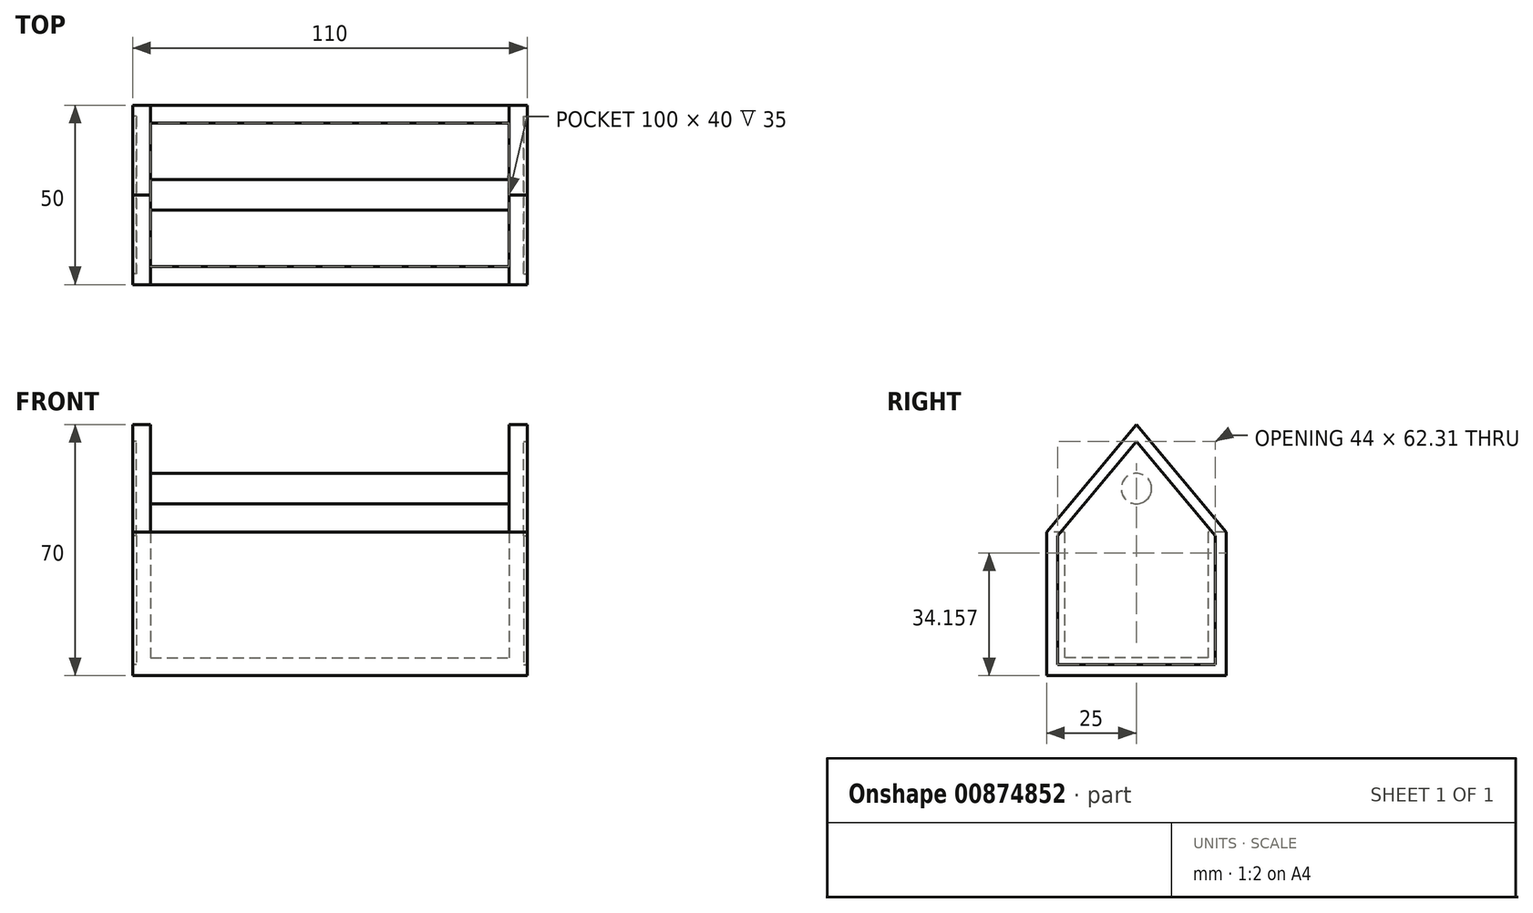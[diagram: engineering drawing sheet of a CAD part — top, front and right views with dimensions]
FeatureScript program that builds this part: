
annotation { "Feature Type Name" : "Feature", "Feature Type Description" : "" }
export const myFeature = defineFeature(function(context is Context, id is Id, definition is map)
    precondition{}
    {
        {
            var Q0;
            Q0=qCreatedBy(makeId("Top.planeOp"),FACE);
            var sketch = newSketch(context, id + "F0", { "sketchPlane" : qUnion([Q0])});
            skLineSegment(sketch, "E0.bottom", {"start": v(-50.43, 19.12) * mm, "end": v(59.57, 19.12) * mm});
            skLineSegment(sketch, "E0.top", {"start": v(-50.43, -30.88) * mm, "end": v(59.57, -30.88) * mm});
            skLineSegment(sketch, "E0.left", {"start": v(-50.43, 19.12) * mm, "end": v(-50.43, -30.88) * mm});
            skLineSegment(sketch, "E0.right", {"start": v(59.57, 19.12) * mm, "end": v(59.57, -30.88) * mm});
            skSolve(sketch);
        }
        {
            var Q0;
            Q0 = qSketchRegion(id + "F0", true);
            extrude(context, id + "F1", {"entities" : qUnion([Q0]), "depth" : 5 * mm, "offsetDistance" : 25 * mm});
        }
        {
            var Q0;
            Q0=makeQuery(id+"F1.opExtrude","CAP_FACE",FACE,{"disambiguationData":[OSD([sQuery(id+"F0.wireOp",EDGE,"E0.bottom"),sQuery(id+"F0.wireOp",EDGE,"E0.top"),sQuery(id+"F0.wireOp",EDGE,"E0.left"),sQuery(id+"F0.wireOp",EDGE,"E0.right")])],"isStart":false});
            var sketch = newSketch(context, id + "F2", { "sketchPlane" : qUnion([Q0])});
            skLineSegment(sketch, "E1.bottom", {"start": v(-50.43, 19.12) * mm, "end": v(59.57, 19.12) * mm});
            skLineSegment(sketch, "E1.top", {"start": v(-50.43, 14.12) * mm, "end": v(59.57, 14.12) * mm});
            skLineSegment(sketch, "E1.left", {"start": v(-50.43, 19.12) * mm, "end": v(-50.43, 14.12) * mm});
            skLineSegment(sketch, "E1.right", {"start": v(59.57, 19.12) * mm, "end": v(59.57, 14.12) * mm});
            skLineSegment(sketch, "E2.bottom", {"start": v(59.57, -30.88) * mm, "end": v(-50.43, -30.88) * mm});
            skLineSegment(sketch, "E2.top", {"start": v(59.57, -25.88) * mm, "end": v(-50.43, -25.88) * mm});
            skLineSegment(sketch, "E2.left", {"start": v(59.57, -30.88) * mm, "end": v(59.57, -25.88) * mm});
            skLineSegment(sketch, "E2.right", {"start": v(-50.43, -30.88) * mm, "end": v(-50.43, -25.88) * mm});
            skLineSegment(sketch, "E3.bottom", {"start": v(-50.43, 14.12) * mm, "end": v(-45.43, 14.12) * mm});
            skLineSegment(sketch, "E3.top", {"start": v(-50.43, -25.88) * mm, "end": v(-45.43, -25.88) * mm});
            skLineSegment(sketch, "E3.left", {"start": v(-50.43, 14.12) * mm, "end": v(-50.43, -25.88) * mm});
            skLineSegment(sketch, "E3.right", {"start": v(-45.43, 14.12) * mm, "end": v(-45.43, -25.88) * mm});
            skLineSegment(sketch, "E4.bottom", {"start": v(59.57, 14.12) * mm, "end": v(54.57, 14.12) * mm});
            skLineSegment(sketch, "E4.top", {"start": v(59.57, -25.88) * mm, "end": v(54.57, -25.88) * mm});
            skLineSegment(sketch, "E4.left", {"start": v(59.57, 14.12) * mm, "end": v(59.57, -25.88) * mm});
            skLineSegment(sketch, "E4.right", {"start": v(54.57, 14.12) * mm, "end": v(54.57, -25.88) * mm});
            skSolve(sketch);
        }
        {
            var Q0;
            Q0 = qSketchRegion(id + "F2", true);
            extrude(context, id + "F3", {"entities" : qUnion([Q0]), "operationType" : NewBodyOperationType.ADD, "depth" : 35 * mm, "offsetDistance" : 25 * mm});
        }
        {
            var Q0;
            Q0=makeQuery(id+"F3.boolean.opBoolean","MERGE",FACE,{"derivedFrom":[makeQuery(id+"F1.opExtrude","SWEPT_FACE",FACE,{"disambiguationData":[OSD([sQuery(id+"F0.wireOp",EDGE,"E0.left")])]}),makeQuery(id+"F3.opExtrude","SWEPT_FACE",FACE,{"disambiguationData":[OSD([sQuery(id+"F2.wireOp",EDGE,"E1.left"),sQuery(id+"F2.wireOp",EDGE,"E2.right"),sQuery(id+"F2.wireOp",EDGE,"E3.left")])]})]});
            var sketch = newSketch(context, id + "F4", { "sketchPlane" : qUnion([Q0])});
            skLineSegment(sketch, "E5", {"start": v(-19.12, 40) * mm, "end": v(5.88, 70) * mm});
            skLineSegment(sketch, "E6", {"start": v(5.88, 70) * mm, "end": v(5.88, 40) * mm});
            skLineSegment(sketch, "E7", {"start": v(30.88, 40) * mm, "end": v(5.88, 70) * mm});
            skSolve(sketch);
        }
        {
            var Q0;
            Q0 = qSketchRegion(id + "F4", true);
            var Q1;
            {var subQ0=sQuery(id+"F4.wireOp",EDGE,"E6");Q1=makeQuery(id+"F4.imprint","IMPRINT",FACE,{"disambiguationData":[TD([[makeQuery(id+"F4.imprint","IMPRINT",EDGE,{"derivedFrom":subQ0}),1.0]])]});}
            var Q2;
            {var subQ0=sQuery(id+"F4.wireOp",EDGE,"E5");Q2=makeQuery(id+"F4.imprint","IMPRINT",FACE,{"disambiguationData":[TD([[makeQuery(id+"F4.imprint","IMPRINT",EDGE,{"derivedFrom":subQ0}),-1.0]])]});}
            extrude(context, id + "F5", {"entities" : qUnion([Q0, Q1, Q2]), "operationType" : NewBodyOperationType.ADD, "oppositeDirection" : true, "depth" : 5 * mm, "offsetDistance" : 25 * mm});
        }
        {
            var Q0;
            Q0=makeQuery(id+"F3.boolean.opBoolean","MERGE",FACE,{"derivedFrom":[makeQuery(id+"F1.opExtrude","SWEPT_FACE",FACE,{"disambiguationData":[OSD([sQuery(id+"F0.wireOp",EDGE,"E0.right")])]}),makeQuery(id+"F3.opExtrude","SWEPT_FACE",FACE,{"disambiguationData":[OSD([sQuery(id+"F2.wireOp",EDGE,"E1.right"),sQuery(id+"F2.wireOp",EDGE,"E2.left"),sQuery(id+"F2.wireOp",EDGE,"E4.left")])]})]});
            var sketch = newSketch(context, id + "F6", { "sketchPlane" : qUnion([Q0])});
            skLineSegment(sketch, "E8", {"start": v(-5.88, 40) * mm, "end": v(-5.88, 70) * mm});
            skLineSegment(sketch, "E9", {"start": v(-5.88, 70) * mm, "end": v(-30.88, 40) * mm});
            skLineSegment(sketch, "E10", {"start": v(19.12, 40) * mm, "end": v(-5.88, 70) * mm});
            skSolve(sketch);
        }
        {
            var Q0;
            Q0 = qSketchRegion(id + "F6", true);
            var Q1;
            {var subQ0=sQuery(id+"F6.wireOp",EDGE,"E8");Q1=makeQuery(id+"F6.imprint","IMPRINT",FACE,{"disambiguationData":[TD([[makeQuery(id+"F6.imprint","IMPRINT",EDGE,{"derivedFrom":subQ0}),1.0]])]});}
            var Q2;
            {var subQ0=sQuery(id+"F6.wireOp",EDGE,"E8");Q2=makeQuery(id+"F6.imprint","IMPRINT",FACE,{"disambiguationData":[TD([[makeQuery(id+"F6.imprint","IMPRINT",EDGE,{"derivedFrom":subQ0}),-1.0]])]});}
            extrude(context, id + "F7", {"entities" : qUnion([Q0, Q1, Q2]), "operationType" : NewBodyOperationType.ADD, "oppositeDirection" : true, "depth" : 5 * mm, "offsetDistance" : 25 * mm});
        }
        {
            var Q0;
            Q0=makeQuery(id+"F5.boolean.opBoolean","MERGE",FACE,{"derivedFrom":[makeQuery(id+"F3.opExtrude","SWEPT_FACE",FACE,{"disambiguationData":[OSD([sQuery(id+"F2.wireOp",EDGE,"E3.right")])]}),makeQuery(id+"F5.opExtrude","CAP_FACE",FACE,{"disambiguationData":[OSD([sQuery(id+"F2.wireOp",EDGE,"E1.left"),sQuery(id+"F2.wireOp",EDGE,"E2.right"),sQuery(id+"F2.wireOp",EDGE,"E3.left"),sQuery(id+"F4.wireOp",EDGE,"E5"),sQuery(id+"F4.wireOp",EDGE,"E7")])],"isStart":false})]});
            var sketch = newSketch(context, id + "F8", { "sketchPlane" : qUnion([Q0])});
            skLineSegment(sketch, "E11", {"start": v(-5.88, 70) * mm, "end": v(-5.88, 34.24) * mm});
            skCircle(sketch, "E12", {"center": v(-5.88, 52.12) * mm, "radius": 4.25 * mm});
            skSolve(sketch);
        }
        {
            var Q0;
            Q0 = qSketchRegion(id + "F8", true);
            extrude(context, id + "F9", {"entities" : qUnion([Q0]), "operationType" : NewBodyOperationType.ADD, "depth" : 101 * mm, "offsetDistance" : 25 * mm});
        }
        {
            var Q0;
            {var subQ0=sQuery(id+"F2.wireOp",EDGE,"E4.left");var subQ1=sQuery(id+"F2.wireOp",EDGE,"E2.left");var subQ2=sQuery(id+"F2.wireOp",EDGE,"E1.right");Q0=makeQuery(id+"F7.boolean.opBoolean","MERGE",FACE,{"derivedFrom":[makeQuery(id+"F3.boolean.opBoolean","MERGE",FACE,{"derivedFrom":[makeQuery(id+"F1.opExtrude","SWEPT_FACE",FACE,{"disambiguationData":[OSD([sQuery(id+"F0.wireOp",EDGE,"E0.right")])]}),makeQuery(id+"F3.opExtrude","SWEPT_FACE",FACE,{"disambiguationData":[OSD([subQ2,subQ1,subQ0])]})]}),makeQuery(id+"F7.opExtrude","CAP_FACE",FACE,{"disambiguationData":[OSD([subQ2,subQ1,subQ0,sQuery(id+"F6.wireOp",EDGE,"E9"),sQuery(id+"F6.wireOp",EDGE,"E10")])],"isStart":true})]});}
            var sketch = newSketch(context, id + "F10", { "sketchPlane" : qUnion([Q0])});
            skLineSegment(sketch, "E13", {"start": v(-27.88, 3) * mm, "end": v(16.12, 3) * mm});
            skLineSegment(sketch, "E14", {"start": v(16.12, 3) * mm, "end": v(16.12, 38.91) * mm});
            skLineSegment(sketch, "E15", {"start": v(16.12, 38.91) * mm, "end": v(-5.88, 65.31) * mm});
            skLineSegment(sketch, "E16", {"start": v(-5.88, 65.31) * mm, "end": v(-27.88, 38.91) * mm});
            skLineSegment(sketch, "E17", {"start": v(-27.88, 38.91) * mm, "end": v(-27.88, 3) * mm});
            skSolve(sketch);
        }
        {
            var Q0;
            Q0 = qSketchRegion(id + "F10", true);
            extrude(context, id + "F11", {"entities" : qUnion([Q0]), "operationType" : NewBodyOperationType.REMOVE, "oppositeDirection" : true, "depth" : 1 * mm, "offsetDistance" : 25 * mm});
        }
        {
            var Q0;
            {var subQ0=sQuery(id+"F2.wireOp",EDGE,"E3.left");var subQ1=sQuery(id+"F2.wireOp",EDGE,"E2.right");var subQ2=sQuery(id+"F2.wireOp",EDGE,"E1.left");Q0=makeQuery(id+"F5.boolean.opBoolean","MERGE",FACE,{"derivedFrom":[makeQuery(id+"F3.boolean.opBoolean","MERGE",FACE,{"derivedFrom":[makeQuery(id+"F1.opExtrude","SWEPT_FACE",FACE,{"disambiguationData":[OSD([sQuery(id+"F0.wireOp",EDGE,"E0.left")])]}),makeQuery(id+"F3.opExtrude","SWEPT_FACE",FACE,{"disambiguationData":[OSD([subQ2,subQ1,subQ0])]})]}),makeQuery(id+"F5.opExtrude","CAP_FACE",FACE,{"disambiguationData":[OSD([subQ2,subQ1,subQ0,sQuery(id+"F4.wireOp",EDGE,"E5"),sQuery(id+"F4.wireOp",EDGE,"E7")])],"isStart":true})]});}
            var sketch = newSketch(context, id + "F12", { "sketchPlane" : qUnion([Q0])});
            skLineSegment(sketch, "E18", {"start": v(-16.12, 3) * mm, "end": v(27.88, 3) * mm});
            skLineSegment(sketch, "E19", {"start": v(27.88, 3) * mm, "end": v(27.88, 38.91) * mm});
            skLineSegment(sketch, "E20", {"start": v(27.88, 38.91) * mm, "end": v(5.88, 65.31) * mm});
            skLineSegment(sketch, "E21", {"start": v(5.88, 65.31) * mm, "end": v(-16.12, 38.91) * mm});
            skLineSegment(sketch, "E22", {"start": v(-16.12, 38.91) * mm, "end": v(-16.12, 3) * mm});
            skSolve(sketch);
        }
        {
            var Q0;
            Q0 = qSketchRegion(id + "F12", true);
            extrude(context, id + "F13", {"entities" : qUnion([Q0]), "operationType" : NewBodyOperationType.REMOVE, "oppositeDirection" : true, "depth" : 1 * mm, "offsetDistance" : 25 * mm});
        }
    });
